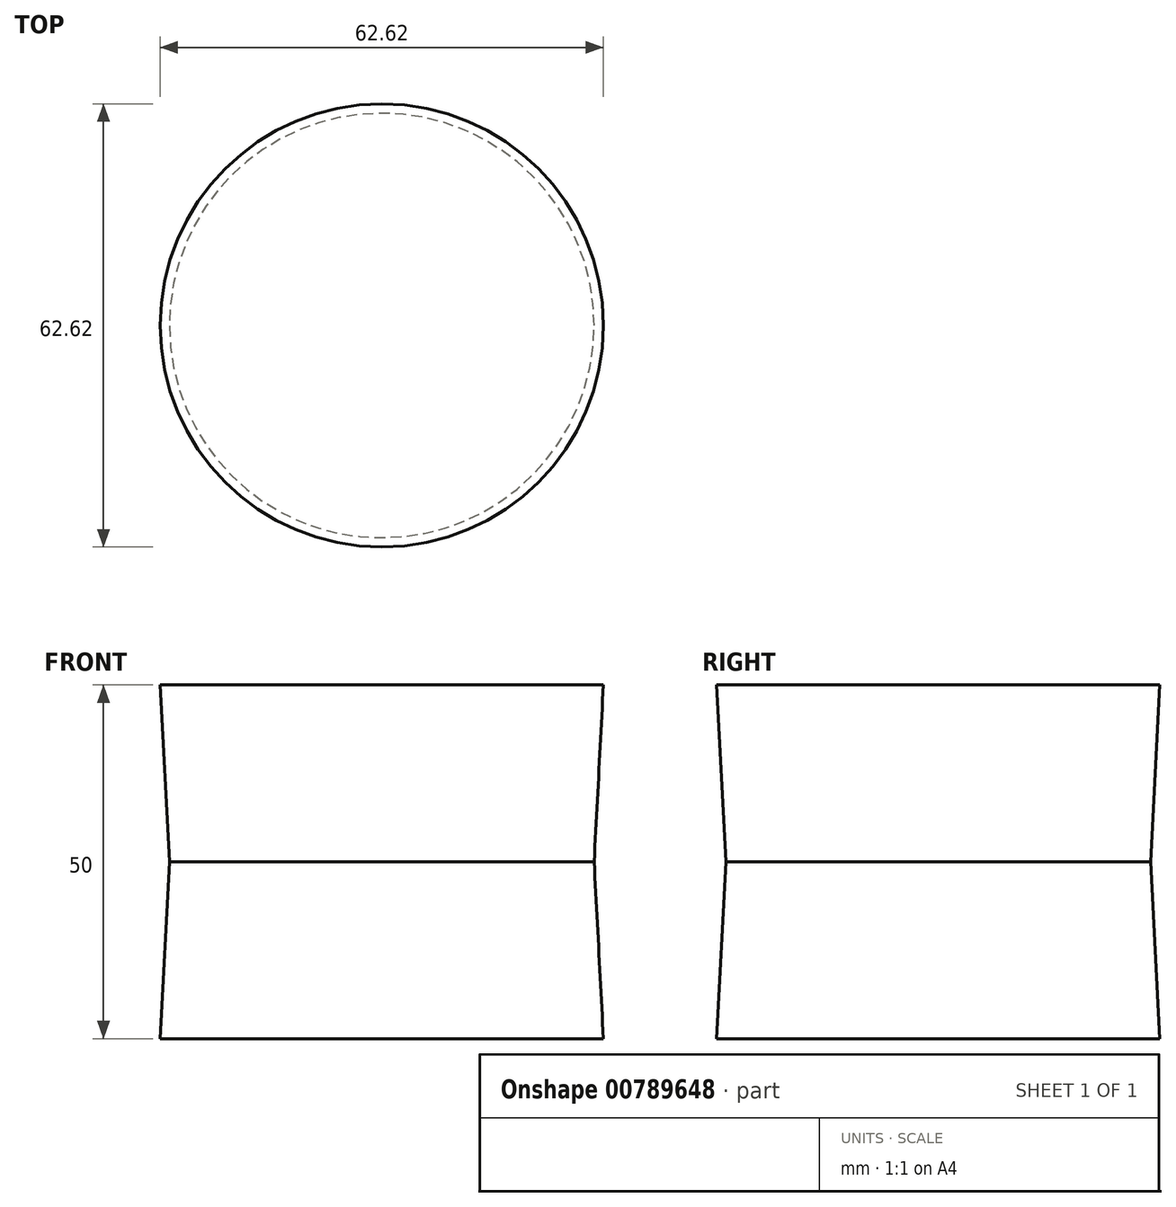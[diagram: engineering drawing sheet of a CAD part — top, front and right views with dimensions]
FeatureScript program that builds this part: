
annotation { "Feature Type Name" : "Feature", "Feature Type Description" : "" }
export const myFeature = defineFeature(function(context is Context, id is Id, definition is map)
    precondition{}
    {
        {
            var Q0;
            Q0=qCreatedBy(makeId("Top.planeOp"),FACE);
            var sketch = newSketch(context, id + "F0", { "sketchPlane" : qUnion([Q0])});
            skCircle(sketch, "E0", {"center": v(0, 0) * mm, "radius": 30 * mm});
            skSolve(sketch);
        }
        {
            var Q0;
            Q0=makeQuery(id+"F0.imprint","IMPRINT",FACE,{"disambiguationData":[TD([[makeQuery(id+"F0.imprint","IMPRINT",EDGE,{"derivedFrom":sQuery(id+"F0.wireOp",EDGE,"E0")}),1.0]])]});
            extrude(context, id + "F1", {"entities" : qUnion([Q0]), "endBound" : BoundingType.SYMMETRIC, "depth" : 50 * mm, "offsetDistance" : 25 * mm, "hasDraft" : true, "draftAngle" : 3 * degree});
        }
    });
